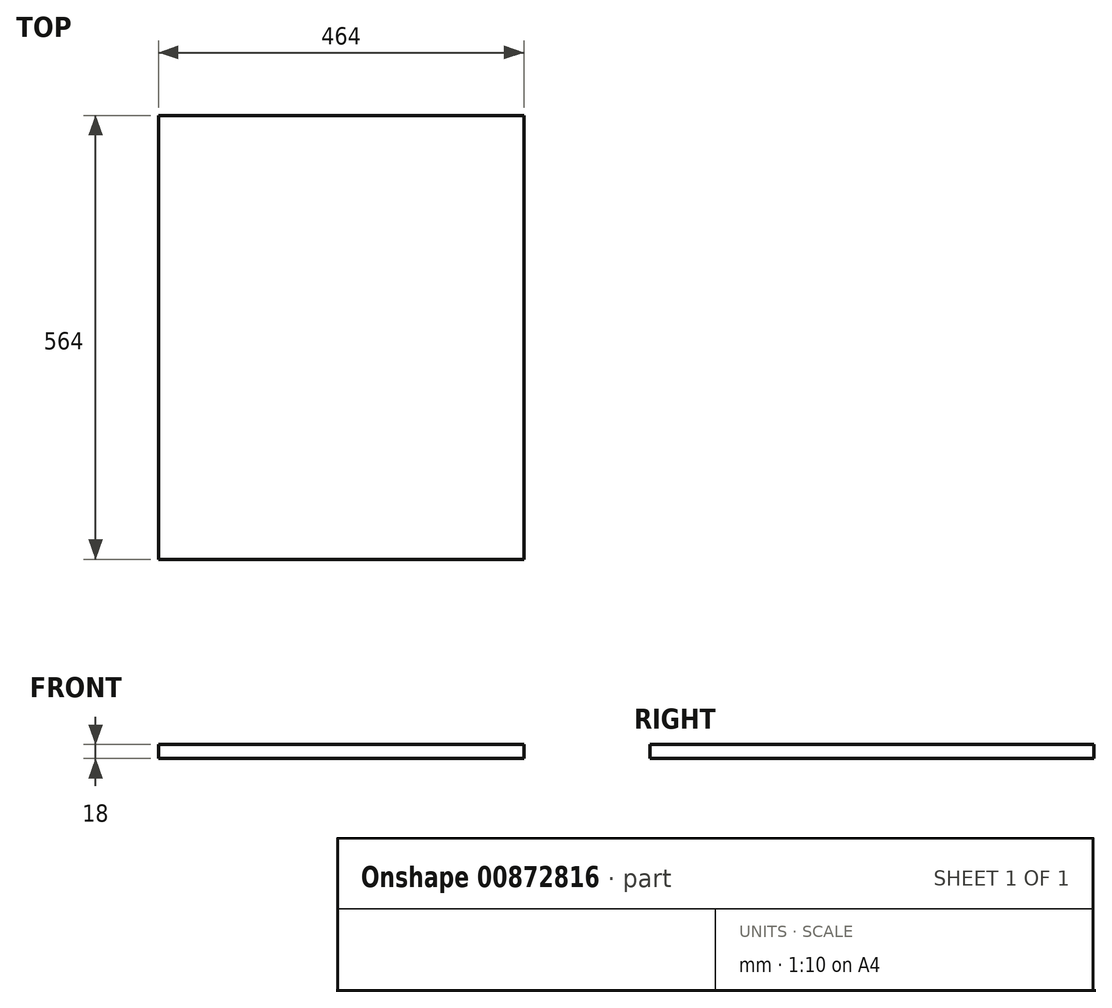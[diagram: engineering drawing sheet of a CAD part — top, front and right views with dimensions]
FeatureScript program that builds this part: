
annotation { "Feature Type Name" : "Feature", "Feature Type Description" : "" }
export const myFeature = defineFeature(function(context is Context, id is Id, definition is map)
    precondition{}
    {
        {
            var Q0;
            Q0=qCreatedBy(makeId("Top.planeOp"),FACE);
            var sketch = newSketch(context, id + "F0", { "sketchPlane" : qUnion([Q0])});
            skLineSegment(sketch, "E0.bottom", {"start": v(232, -282) * mm, "end": v(-232, -282) * mm});
            skLineSegment(sketch, "E0.top", {"start": v(232, 282) * mm, "end": v(-232, 282) * mm});
            skLineSegment(sketch, "E0.left", {"start": v(232, -282) * mm, "end": v(232, 282) * mm});
            skLineSegment(sketch, "E0.right", {"start": v(-232, -282) * mm, "end": v(-232, 282) * mm});
            skPoint(sketch, "E0.middle", {"position": v(0, 0) * mm});
            skSolve(sketch);
        }
        {
            var Q0;
            Q0 = qSketchRegion(id + "F0", true);
            extrude(context, id + "F1", {"entities" : qUnion([Q0]), "depth" : 18 * mm, "offsetDistance" : 25 * mm});
        }
    });
